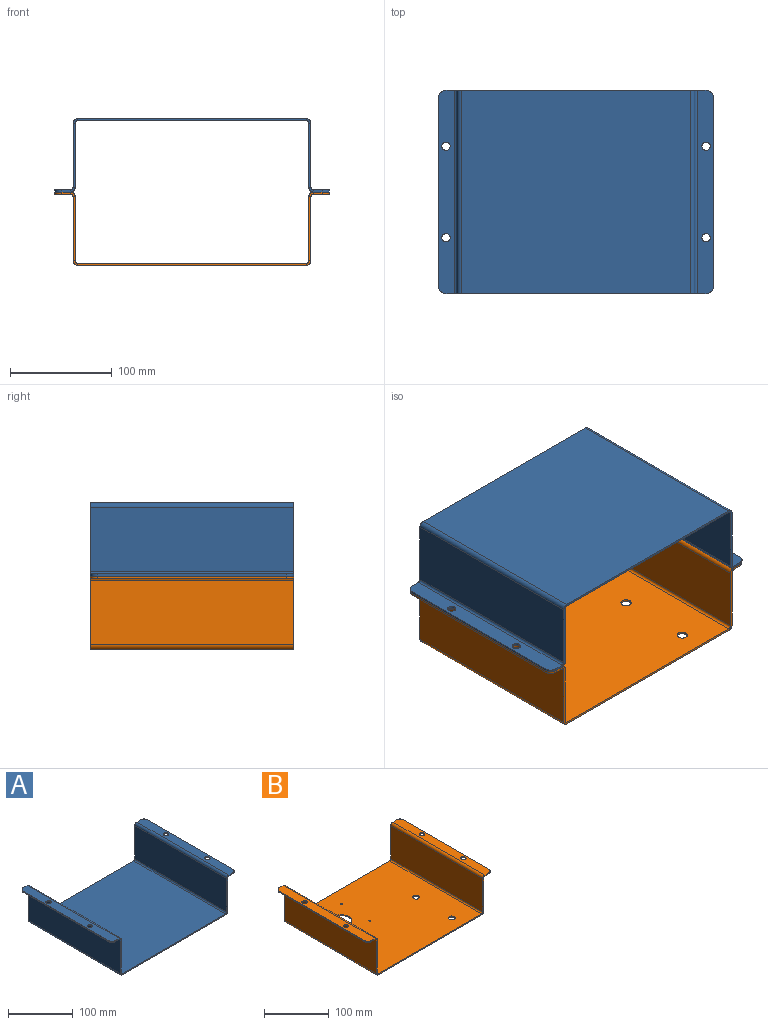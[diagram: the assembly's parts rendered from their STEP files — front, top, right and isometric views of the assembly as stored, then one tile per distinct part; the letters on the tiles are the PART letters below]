
ASSEMBLY  parts=2 mates=1
PART A: 46 faces, bbox 270x200x72 mm
  f0: plane 225.4x2mm, normal (0,1,0), area 450.8mm2, adj f2,f3,f22,f43
  f1: plane 225.4x2mm, normal (0,-1,0), area 450.8mm2, adj f2,f3,f21,f42
  f2: plane 225.4x200mm, normal (0,0,-1), area 45080mm2, adj f0,f1,f23,f44
  f3: plane 225.4x200mm, normal (0,0,1), area 45080mm2, adj f0,f1,f24,f45
  f4: plane 63.4x2mm, normal (0,1,0), area 126.8mm2, adj f6,f7,f18,f22
  f5: plane 63.4x2mm, normal (0,-1,0), area 126.8mm2, adj f6,f7,f17,f21
  f6: plane 200x63.4mm, normal (-1,0,0), area 12680mm2, adj f4,f5,f20,f23
  f7: plane 200x63.4mm, normal (1,0,0), area 12680mm2, adj f4,f5,f19,f24
  f8: plane 8.6x2mm, normal (0,1,0), area 17.2mm2, adj f13,f14,f16,f18
  f9: plane 8.6x2mm, normal (0,-1,0), area 17.2mm2, adj f13,f14,f15,f17
  f10: cylinder r=4.1mm len=8.2mm, axis (0,0,-1), area 51.5mm2, adj f13,f14
  f11: cylinder r=4.1mm len=8.2mm, axis (0,0,-1), area 51.5mm2, adj f13,f14
  f12: plane 185.8x2mm, normal (-1,0,0), area 371.6mm2, adj f13,f14,f15,f16
  f13: plane 200x15.7mm, normal (0,0,-1), area 3012.7mm2, adj f8,f9,f10,f11,f12,f15,f16,f20
  f14: plane 200x15.7mm, normal (0,0,1), area 3012.7mm2, adj f8,f9,f10,f11,f12,f15,f16,f19
  f15: cylinder r=7.1mm len=7.1mm, axis (0,0,1), area 22.3mm2, adj f9,f12,f13,f14
  f16: cylinder r=7.1mm len=7.1mm, axis (0,0,-1), area 22.3mm2, adj f8,f12,f13,f14
  f17: plane 4.3x4.3mm, normal (0,-1,0), area 10.4mm2, adj f5,f9,f19,f20
  f18: plane 4.3x4.3mm, normal (0,1,0), area 10.4mm2, adj f4,f8,f19,f20
  f19: cylinder r=4.3mm len=200mm, axis (0,-1,0), area 1350.9mm2, adj f7,f14,f17,f18
  f20: cylinder r=2.3mm len=200mm, axis (0,-1,0), area 722.6mm2, adj f6,f13,f17,f18
  f21: plane 4.3x4.3mm, normal (0,-1,0), area 10.4mm2, adj f1,f5,f23,f24
  f22: plane 4.3x4.3mm, normal (0,1,0), area 10.4mm2, adj f0,f4,f23,f24
  f23: cylinder r=4.3mm len=200mm, axis (0,-1,0), area 1350.9mm2, adj f2,f6,f21,f22
  f24: cylinder r=2.3mm len=200mm, axis (0,-1,0), area 722.6mm2, adj f3,f7,f21,f22
  f25: plane 63.4x2mm, normal (0,1,0), area 126.8mm2, adj f27,f28,f39,f43
  f26: plane 63.4x2mm, normal (0,-1,0), area 126.8mm2, adj f27,f28,f38,f42
  f27: plane 200x63.4mm, normal (1,0,0), area 12680mm2, adj f25,f26,f41,f44
  f28: plane 200x63.4mm, normal (-1,0,0), area 12680mm2, adj f25,f26,f40,f45
  f29: plane 8.6x2mm, normal (0,1,0), area 17.2mm2, adj f34,f35,f36,f39
  f30: plane 185.8x2mm, normal (1,0,0), area 371.6mm2, adj f34,f35,f36,f37
  f31: plane 8.6x2mm, normal (0,-1,0), area 17.2mm2, adj f34,f35,f37,f38
  f32: cylinder r=4.1mm len=8.2mm, axis (0,0,-1), area 51.5mm2, adj f34,f35
  f33: cylinder r=4.1mm len=8.2mm, axis (0,0,-1), area 51.5mm2, adj f34,f35
  f34: plane 200x15.7mm, normal (0,0,-1), area 3012.7mm2, adj f29,f30,f31,f32,f33,f36,f37,f41
  f35: plane 200x15.7mm, normal (0,0,1), area 3012.7mm2, adj f29,f30,f31,f32,f33,f36,f37,f40
  f36: cylinder r=7.1mm len=7.1mm, axis (0,0,-1), area 22.3mm2, adj f29,f30,f34,f35
  f37: cylinder r=7.1mm len=7.1mm, axis (0,0,1), area 22.3mm2, adj f30,f31,f34,f35
  f38: plane 4.3x4.3mm, normal (0,-1,0), area 10.4mm2, adj f26,f31,f40,f41
  f39: plane 4.3x4.3mm, normal (0,1,0), area 10.4mm2, adj f25,f29,f40,f41
  f40: cylinder r=4.3mm len=200mm, axis (0,-1,0), area 1350.9mm2, adj f28,f35,f38,f39
  f41: cylinder r=2.3mm len=200mm, axis (0,-1,0), area 722.6mm2, adj f27,f34,f38,f39
  f42: plane 4.3x4.3mm, normal (0,-1,0), area 10.4mm2, adj f1,f26,f44,f45
  f43: plane 4.3x4.3mm, normal (0,1,0), area 10.4mm2, adj f0,f25,f44,f45
  f44: cylinder r=4.3mm len=200mm, axis (0,-1,0), area 1350.9mm2, adj f2,f27,f42,f43
  f45: cylinder r=2.3mm len=200mm, axis (0,-1,0), area 722.6mm2, adj f3,f28,f42,f43
PART B: 53 faces, bbox 270x200x72 mm
  f0: plane 225.4x2mm, normal (0,1,0), area 450.8mm2, adj f9,f10,f29,f50
  f1: plane 225.4x2mm, normal (0,-1,0), area 450.8mm2, adj f9,f10,f28,f49
  f2: cylinder r=5.1mm len=10.2mm, axis (0,0,-1), area 64.1mm2, adj f9,f10
  f3: cylinder r=5.1mm len=10.2mm, axis (0,0,-1), area 64.1mm2, adj f9,f10
  f4: cylinder r=1.65mm len=3.3mm, axis (0,0,-1), area 20.7mm2, adj f9,f10
  f5: cylinder r=1.65mm len=3.3mm, axis (0,0,-1), area 20.7mm2, adj f9,f10
  f6: cylinder r=1.65mm len=3.3mm, axis (0,0,-1), area 20.7mm2, adj f9,f10
  f7: cylinder r=1.65mm len=3.3mm, axis (0,0,-1), area 20.7mm2, adj f9,f10
  f8: cylinder r=15.85mm len=31.71mm, axis (0,0,-1), area 199.2mm2, adj f9,f10
  f9: plane 225.4x200mm, normal (0,0,-1), area 44092.7mm2, adj f0,f1,f2,f3,f4,f5,f6,f7
  f10: plane 225.4x200mm, normal (0,0,1), area 44092.7mm2, adj f0,f1,f2,f3,f4,f5,f6,f7
  f11: plane 63.4x2mm, normal (0,1,0), area 126.8mm2, adj f13,f14,f25,f29
  f12: plane 63.4x2mm, normal (0,-1,0), area 126.8mm2, adj f13,f14,f24,f28
  f13: plane 200x63.4mm, normal (-1,0,0), area 12680mm2, adj f11,f12,f27,f30
  f14: plane 200x63.4mm, normal (1,0,0), area 12680mm2, adj f11,f12,f26,f31
  f15: plane 8.6x2mm, normal (0,1,0), area 17.2mm2, adj f20,f21,f23,f25
  f16: plane 8.6x2mm, normal (0,-1,0), area 17.2mm2, adj f20,f21,f22,f24
  f17: cylinder r=4.1mm len=8.2mm, axis (0,0,-1), area 51.5mm2, adj f20,f21
  f18: cylinder r=4.1mm len=8.2mm, axis (0,0,-1), area 51.5mm2, adj f20,f21
  f19: plane 185.8x2mm, normal (-1,0,0), area 371.6mm2, adj f20,f21,f22,f23
  f20: plane 200x15.7mm, normal (0,0,-1), area 3012.7mm2, adj f15,f16,f17,f18,f19,f22,f23,f27
  f21: plane 200x15.7mm, normal (0,0,1), area 3012.7mm2, adj f15,f16,f17,f18,f19,f22,f23,f26
  f22: cylinder r=7.1mm len=7.1mm, axis (0,0,1), area 22.3mm2, adj f16,f19,f20,f21
  f23: cylinder r=7.1mm len=7.1mm, axis (0,0,-1), area 22.3mm2, adj f15,f19,f20,f21
  f24: plane 4.3x4.3mm, normal (0,-1,0), area 10.4mm2, adj f12,f16,f26,f27
  f25: plane 4.3x4.3mm, normal (0,1,0), area 10.4mm2, adj f11,f15,f26,f27
  f26: cylinder r=4.3mm len=200mm, axis (0,-1,0), area 1350.9mm2, adj f14,f21,f24,f25
  f27: cylinder r=2.3mm len=200mm, axis (0,-1,0), area 722.6mm2, adj f13,f20,f24,f25
  f28: plane 4.3x4.3mm, normal (0,-1,0), area 10.4mm2, adj f1,f12,f30,f31
  f29: plane 4.3x4.3mm, normal (0,1,0), area 10.4mm2, adj f0,f11,f30,f31
  f30: cylinder r=4.3mm len=200mm, axis (0,-1,0), area 1350.9mm2, adj f9,f13,f28,f29
  f31: cylinder r=2.3mm len=200mm, axis (0,-1,0), area 722.6mm2, adj f10,f14,f28,f29
  f32: plane 63.4x2mm, normal (0,1,0), area 126.8mm2, adj f34,f35,f46,f50
  f33: plane 63.4x2mm, normal (0,-1,0), area 126.8mm2, adj f34,f35,f45,f49
  f34: plane 200x63.4mm, normal (1,0,0), area 12680mm2, adj f32,f33,f48,f51
  f35: plane 200x63.4mm, normal (-1,0,0), area 12680mm2, adj f32,f33,f47,f52
  f36: plane 8.6x2mm, normal (0,1,0), area 17.2mm2, adj f41,f42,f43,f46
  f37: plane 185.8x2mm, normal (1,0,0), area 371.6mm2, adj f41,f42,f43,f44
  f38: plane 8.6x2mm, normal (0,-1,0), area 17.2mm2, adj f41,f42,f44,f45
  f39: cylinder r=4.1mm len=8.2mm, axis (0,0,-1), area 51.5mm2, adj f41,f42
  f40: cylinder r=4.1mm len=8.2mm, axis (0,0,-1), area 51.5mm2, adj f41,f42
  f41: plane 200x15.7mm, normal (0,0,-1), area 3012.7mm2, adj f36,f37,f38,f39,f40,f43,f44,f48
  f42: plane 200x15.7mm, normal (0,0,1), area 3012.7mm2, adj f36,f37,f38,f39,f40,f43,f44,f47
  f43: cylinder r=7.1mm len=7.1mm, axis (0,0,-1), area 22.3mm2, adj f36,f37,f41,f42
  f44: cylinder r=7.1mm len=7.1mm, axis (0,0,1), area 22.3mm2, adj f37,f38,f41,f42
  f45: plane 4.3x4.3mm, normal (0,-1,0), area 10.4mm2, adj f33,f38,f47,f48
  f46: plane 4.3x4.3mm, normal (0,1,0), area 10.4mm2, adj f32,f36,f47,f48
  f47: cylinder r=4.3mm len=200mm, axis (0,-1,0), area 1350.9mm2, adj f35,f42,f45,f46
  f48: cylinder r=2.3mm len=200mm, axis (0,-1,0), area 722.6mm2, adj f34,f41,f45,f46
  f49: plane 4.3x4.3mm, normal (0,-1,0), area 10.4mm2, adj f1,f33,f51,f52
  f50: plane 4.3x4.3mm, normal (0,1,0), area 10.4mm2, adj f0,f32,f51,f52
  f51: cylinder r=4.3mm len=200mm, axis (0,-1,0), area 1350.9mm2, adj f9,f34,f49,f50
  f52: cylinder r=2.3mm len=200mm, axis (0,-1,0), area 722.6mm2, adj f10,f35,f49,f50
PLACE A rot(axis=(1,0,0),180deg) t=(-33.89,-80.53,165.3)mm
PLACE B t=(-33.89,119.47,25.3)mm
MATE fastened A.f33 <-> B.f39  axis (0,0,-1) through (94.01,64.47,95.3)mm
